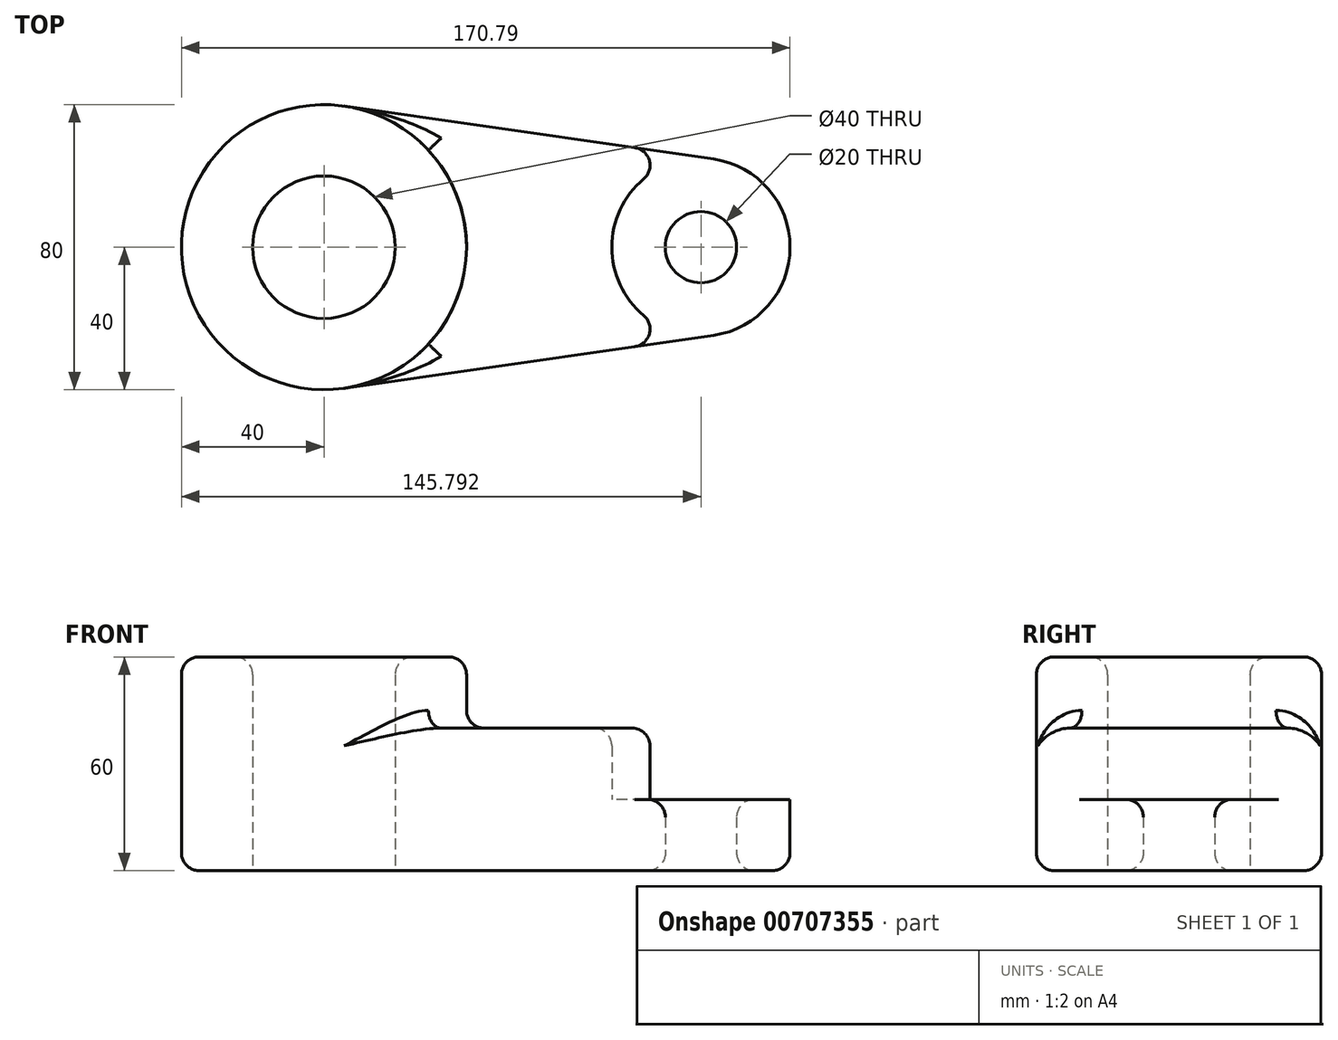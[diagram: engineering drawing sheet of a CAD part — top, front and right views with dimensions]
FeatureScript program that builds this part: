
annotation { "Feature Type Name" : "Feature", "Feature Type Description" : "" }
export const myFeature = defineFeature(function(context is Context, id is Id, definition is map)
    precondition{}
    {
        {
            var Q0;
            Q0=qCreatedBy(makeId("Top.planeOp"),FACE);
            var sketch = newSketch(context, id + "F0", { "sketchPlane" : qUnion([Q0])});
            skCircle(sketch, "E0", {"center": v(-50, 0) * mm, "radius": 20 * mm});
            skCircle(sketch, "E1", {"center": v(-50, 0) * mm, "radius": 40 * mm});
            skCircle(sketch, "E2", {"center": v(55.8, 0) * mm, "radius": 10 * mm});
            skCircle(sketch, "E3", {"center": v(55.8, 0) * mm, "radius": 25 * mm});
            skCircle(sketch, "E4", {"center": v(55.8, 0) * mm, "radius": 1.14 * mm});
            skCircle(sketch, "E5", {"center": v(55.8, 0) * mm, "radius": 1.35 * mm});
            skCircle(sketch, "E6", {"center": v(55.8, 0) * mm, "radius": 1.46 * mm});
            skLineSegment(sketch, "E7", {"start": v(-44.33, 39.6) * mm, "end": v(59.34, 24.75) * mm});
            skLineSegment(sketch, "E8", {"start": v(-44.33, -39.6) * mm, "end": v(59.34, -24.75) * mm});
            skSolve(sketch);
        }
        {
            var Q0;
            Q0=makeQuery(id+"F0.imprint","IMPRINT",FACE,{"disambiguationData":[TD([[makeQuery(id+"F0.imprint","IMPRINT",EDGE,{"derivedFrom":sQuery(id+"F0.wireOp",EDGE,"E0")}),-1.0]])]});
            extrude(context, id + "F1", {"entities" : qUnion([Q0]), "depth" : 60 * mm, "offsetDistance" : 25 * mm});
        }
        {
            var Q0;
            {var subQ0=sQuery(id+"F0.wireOp",EDGE,"E7");Q0=makeQuery(id+"F0.imprint","IMPRINT",FACE,{"disambiguationData":[TD([[makeQuery(id+"F0.imprint","IMPRINT",EDGE,{"derivedFrom":subQ0}),-1.0]])]});}
            extrude(context, id + "F2", {"entities" : qUnion([Q0]), "operationType" : NewBodyOperationType.ADD, "depth" : 40 * mm, "offsetDistance" : 25 * mm});
        }
        {
            var Q0;
            Q0=makeQuery(id+"F0.imprint","IMPRINT",FACE,{"disambiguationData":[TD([[makeQuery(id+"F0.imprint","IMPRINT",EDGE,{"derivedFrom":sQuery(id+"F0.wireOp",EDGE,"E2")}),-1.0]])]});
            extrude(context, id + "F3", {"entities" : qUnion([Q0]), "operationType" : NewBodyOperationType.ADD, "depth" : 20 * mm, "offsetDistance" : 25 * mm});
        }
        {
            var Q0;
            Q0=makeQuery(id+"F1.opExtrude","CAP_FACE",FACE,{"disambiguationData":[OSD([sQuery(id+"F0.wireOp",EDGE,"E0"),sQuery(id+"F0.wireOp",EDGE,"E1")])],"isStart":false});
            var Q1;
            Q1=makeQuery(id+"F2.opExtrude","CAP_FACE",FACE,{"disambiguationData":[OSD([sQuery(id+"F0.wireOp",EDGE,"E1"),sQuery(id+"F0.wireOp",EDGE,"E3"),sQuery(id+"F0.wireOp",EDGE,"E7"),sQuery(id+"F0.wireOp",EDGE,"E8")])],"isStart":false});
            var Q2;
            Q2=makeQuery(id+"F3.opExtrude","CAP_EDGE",EDGE,{"disambiguationData":[OSD([sQuery(id+"F0.wireOp",EDGE,"E2")])],"isStart":true});
            var Q3;
            Q3=makeQuery(id+"F2.opExtrude","SWEPT_FACE",FACE,{"disambiguationData":[OSD([sQuery(id+"F0.wireOp",EDGE,"E7")])]});
            var Q4;
            Q4=makeQuery(id+"F1.opExtrude","SWEPT_FACE",FACE,{"disambiguationData":[OSD([sQuery(id+"F0.wireOp",EDGE,"E1")])]});
            var Q5;
            Q5=makeQuery(id+"F2.opExtrude","SWEPT_FACE",FACE,{"disambiguationData":[OSD([sQuery(id+"F0.wireOp",EDGE,"E8")])]});
            var Q6;
            Q6=makeQuery(id+"F3.opExtrude","CAP_EDGE",EDGE,{"disambiguationData":[OSD([sQuery(id+"F0.wireOp",EDGE,"E2")])],"isStart":false});
            fillet(context, id + "F4", {"entities" : qUnion([Q0, Q1, Q2, Q3, Q4, Q5, Q6]), "radius" : 5 * mm, "tangentPropagation" : true, "allowEdgeOverflow" : false});
        }
    });
